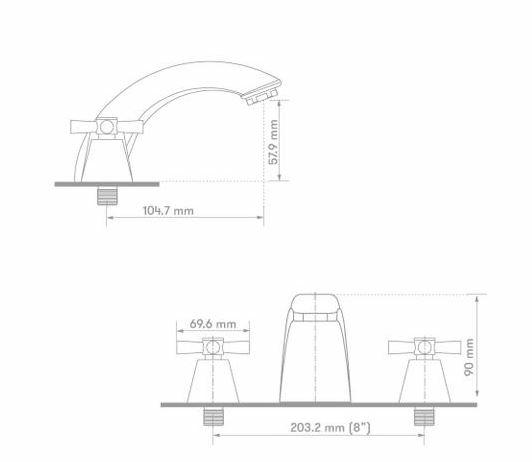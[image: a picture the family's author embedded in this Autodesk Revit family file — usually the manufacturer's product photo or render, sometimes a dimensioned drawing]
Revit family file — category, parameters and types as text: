
# Revit family: 01-0203-11-MEZCLADOR LAVAMANOS COLECCION PORTOBELLO
name_source: partatom
category: Plumbing Fixtures
revit_build: Autodesk Revit 2018 (Build: 20170223_1515(x64)
units: mm (PartAtom-declared; Revit-internal decimal feet)

## family parameters
Cut with Voids When Loaded = No
Host = Face
OmniClass Number = 23.31.11.00
Part Type = Normal
Room Calculation Point = No
Round Connector Dimension = Use Diameter
Shared = No

## types (1)
- 01-0203-11
    Alto = 110 mm
    Ancho = 35 mm
    CW Connection = Yes
    Default Elevation = 0 mm  [stored 0 ft]
    Description = Griferia Monomando baño
    HW Connection = Yes
    Link Ficha Tecnica = http://infotecnica.gricol.com
    Manufacturer = Gricol
    Model = 01-0203-11
    Plastico ABS Cromado = Metal Acero Inoxidable Cromado
    Product Name = MEZCLADOR LAVAMANOS COLECCIÓN PORTOBELLO
    Profundidad = 127 mm
    Type Image = <None>
    URL = https://www.gricol.com
    Vent Connection = No
    Waste Connection = No

note: [stored X ft] marks values corroborated as IEEE doubles in the binary element streams (Revit-internal decimal feet)

## geometry (parser evidence)
native form markers: Blend x2, Sweep x9
no freeform markers — native parametric forms only
